# Revit family: Kitchen_Sinks_hansgrohe_43354CHN-S43-S431-F730-Built-in-sink-410_hfgx
name_source: partatom
category: Plumbing Fixtures
revit_build: Autodesk Revit 2018 (Build: 20170223_1515(x64)
units: mm (PartAtom-declared; Revit-internal decimal feet)

## family parameters
Cut with Voids When Loaded = No
Host = Face
OmniClass Number = 23.31.13.00
OmniClass Title = Sinks
Part Type = Normal
Room Calculation Point = No
Round Connector Dimension = Use Diameter
Shared = No

## types (1)
- 807 Stainless Steel
    BIMobject category = Sinks
    Connector Description = Water Outlet 45 mm
    Default Elevation = 1219 mm
    Description = S43 S431-F730 Built-in sink 410/290 1-hole incl. manual drain kit
    Design country = Germany
    Diameter = 45  [stored 0.147638 ft]
    Edition number = 1
    IFC Classification = Sanitary Terminal
    Manufacturer = Hansgrohe
    Manufacturer country = Germany
    Manufacturer name = hansgrohe
    Material = Hansgrohe - Metal - 807 Stainless Steel
    Material main = Stainless steel
    Model = 43354CHN
    OmniClass Code = 23-31 13 00
    OmniClass Description = Sinks
    Product Guid = 31285aad-0fca-414c-b4a6-21ad1cced08c
    Product SKU = 43354CHN
    Product data url = https://bimobject.com
    Product family = S43
    Product group = Sinks
    Product name = 43354CHN S43 S431-F730 Built-in sink 410/290 1-hole incl. manual drain kit
    Product url = https://www.hansgrohe.com
    QR code = https://bimobject.com
    UNSPSC Code = 30181504
    URL = https://www.hansgrohe.com
    Uniclass 2015 Code = Pr_40_20_96_45
    Uniclass 2015 Name = Kitchen sinks
    Weight Net (Kg) = 7.3

note: [stored X ft] marks values corroborated as IEEE doubles in the binary element streams (Revit-internal decimal feet)

## geometry (parser evidence)
native form markers: Sweep x2
no freeform markers — native parametric forms only
